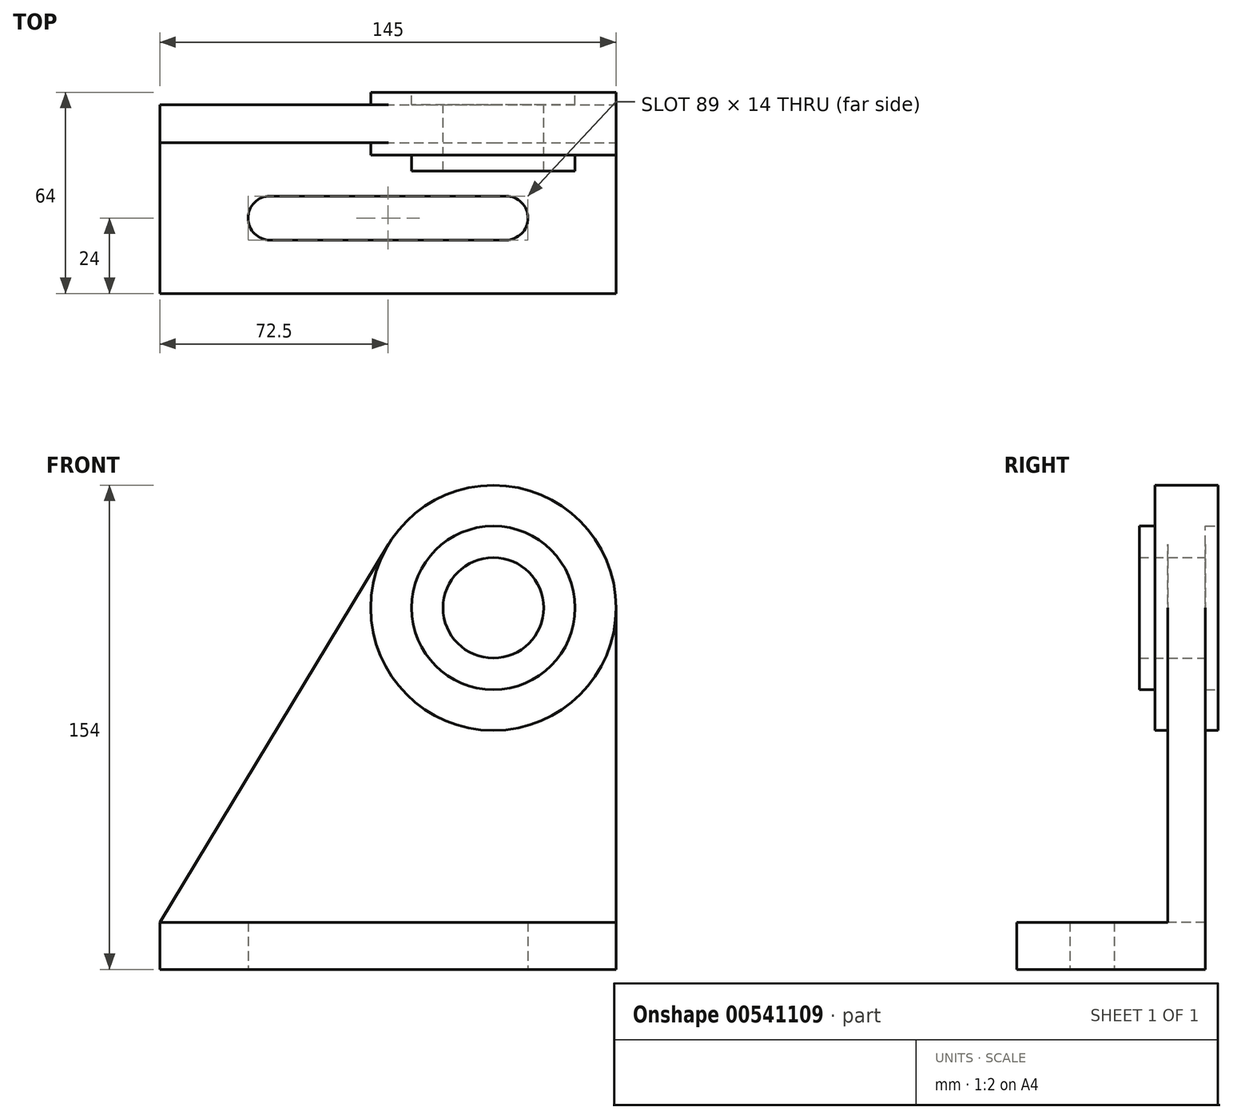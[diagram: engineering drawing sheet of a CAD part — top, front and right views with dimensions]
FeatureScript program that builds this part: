
annotation { "Feature Type Name" : "Feature", "Feature Type Description" : "" }
export const myFeature = defineFeature(function(context is Context, id is Id, definition is map)
    precondition{}
    {
        {
            var Q0;
            Q0=qCreatedBy(makeId("Top.planeOp"),FACE);
            var sketch = newSketch(context, id + "F0", { "sketchPlane" : qUnion([Q0])});
            skLineSegment(sketch, "E0.bottom", {"start": v(-72.5, 0) * mm, "end": v(72.5, 0) * mm});
            skLineSegment(sketch, "E0.top", {"start": v(-72.5, -60) * mm, "end": v(72.5, -60) * mm});
            skLineSegment(sketch, "E0.left", {"start": v(-72.5, 0) * mm, "end": v(-72.5, -60) * mm});
            skLineSegment(sketch, "E0.right", {"start": v(72.5, 0) * mm, "end": v(72.5, -60) * mm});
            skLineSegment(sketch, "E1", {"start": v(-72.5, -12) * mm, "end": v(72.5, -12) * mm});
            skPoint(sketch, "E2", {"position": v(-37.5, -36) * mm});
            skPoint(sketch, "E3", {"position": v(37.5, -36) * mm});
            skArc(sketch, "E4", {"start": v(-37.5, -29) * mm, "mid": v(-44.5, -36) * mm, "end": v(-37.5, -43) * mm});
            skArc(sketch, "E5", {"start": v(37.5, -43) * mm, "mid": v(44.5, -36) * mm, "end": v(37.5, -29) * mm});
            skLineSegment(sketch, "E6", {"start": v(-37.5, -29) * mm, "end": v(37.5, -29) * mm});
            skLineSegment(sketch, "E7", {"start": v(-37.5, -43) * mm, "end": v(37.5, -43) * mm});
            skSolve(sketch);
        }
        {
            var Q0;
            {var subQ1=sQuery(id+"F0.wireOp",EDGE,"E0.top");Q0=makeQuery(id+"F0.imprint","IMPRINT",FACE,{"disambiguationData":[TD([[makeQuery(id+"F0.imprint","IMPRINT",EDGE,{"derivedFrom":subQ1}),1.0]])]});}
            extrude(context, id + "F1", {"entities" : qUnion([Q0]), "depth" : 15 * mm, "offsetDistance" : 25 * mm});
        }
        {
            var Q0;
            {var subQ0=sQuery(id+"F0.wireOp",EDGE,"E0.bottom");Q0=makeQuery(id+"F0.imprint","IMPRINT",FACE,{"disambiguationData":[TD([[makeQuery(id+"F0.imprint","IMPRINT",EDGE,{"derivedFrom":subQ0}),-1.0]])]});}
            extrude(context, id + "F2", {"entities" : qUnion([Q0]), "operationType" : NewBodyOperationType.ADD, "depth" : 15 * mm, "offsetDistance" : 25 * mm});
        }
        {
            var Q0;
            Q0=qCreatedBy(makeId("Front.planeOp"),FACE);
            var sketch = newSketch(context, id + "F3", { "sketchPlane" : qUnion([Q0])});
            skLineSegment(sketch, "E8", {"start": v(-72.5, 0) * mm, "end": v(72.5, 0) * mm});
            skLineSegment(sketch, "E9", {"start": v(72.5, 0) * mm, "end": v(72.5, 115) * mm});
            skCircle(sketch, "E10", {"center": v(33.5, 115) * mm, "radius": 39 * mm});
            skCircle(sketch, "E11", {"center": v(33.5, 115) * mm, "radius": 26 * mm});
            skCircle(sketch, "E12", {"center": v(33.5, 115) * mm, "radius": 16 * mm});
            skLineSegment(sketch, "E13", {"start": v(-72.5, 0) * mm, "end": v(-72.5, 15) * mm});
            skLineSegment(sketch, "E14", {"start": v(-72.5, 15) * mm, "end": v(0.12, 135.17) * mm});
            skSolve(sketch);
        }
        {
            var Q0;
            Q0=makeQuery(id+"F3.imprint","IMPRINT",FACE,{"disambiguationData":[TD([[makeQuery(id+"F3.imprint","IMPRINT",EDGE,{"derivedFrom":sQuery(id+"F3.wireOp",EDGE,"E8")}),1.0]])]});
            extrude(context, id + "F4", {"entities" : qUnion([Q0]), "operationType" : NewBodyOperationType.ADD, "depth" : 12 * mm, "offsetDistance" : 25 * mm});
        }
        {
            var Q0;
            Q0=makeQuery(id+"F3.imprint","IMPRINT",FACE,{"disambiguationData":[TD([[makeQuery(id+"F3.imprint","IMPRINT",EDGE,{"derivedFrom":sQuery(id+"F3.wireOp",EDGE,"E11")}),-1.0]])]});
            extrude(context, id + "F5", {"entities" : qUnion([Q0]), "operationType" : NewBodyOperationType.ADD, "depth" : 16 * mm, "offsetDistance" : 25 * mm, "hasSecondDirection" : true, "secondDirectionOppositeDirection" : true, "secondDirectionDepth" : 4 * mm});
        }
        {
            var Q0;
            Q0=makeQuery(id+"F3.imprint","IMPRINT",FACE,{"disambiguationData":[TD([[makeQuery(id+"F3.imprint","IMPRINT",EDGE,{"derivedFrom":sQuery(id+"F3.wireOp",EDGE,"E11")}),1.0]])]});
            extrude(context, id + "F6", {"entities" : qUnion([Q0]), "operationType" : NewBodyOperationType.ADD, "depth" : 21 * mm, "offsetDistance" : 25 * mm});
        }
    });
